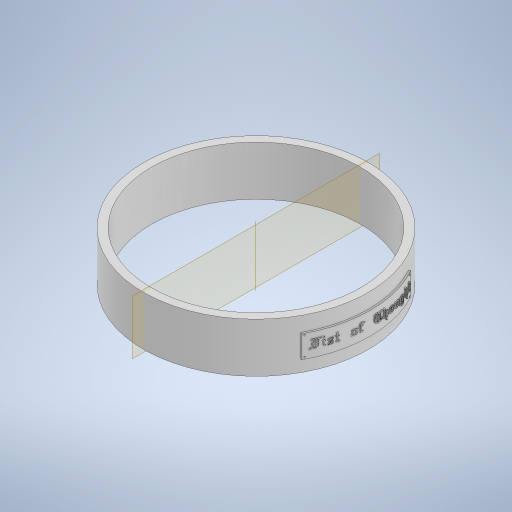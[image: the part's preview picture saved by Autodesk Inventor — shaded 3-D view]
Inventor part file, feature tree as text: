
AUTODESK INVENTOR PART (.ipt)
format: ipt  version: 2023 (Build 270158000, 158)  size: 5,846,016 bytes
history: native  units: in
note: dims shown in document units (in); Inventor stores cm internally (conversion verified against a paired STEP export)
features: emboss x3, pattern_circular x3, other x2, extrude x1, plane x1, fillet x1, sketch x1
ambient origin geometry x8: Origin, YZ Plane, XZ Plane, XY Plane, X Axis, Y Axis, Z Axis, Center Point
bodies: Solid1 (feature_tree)
feature tree (12):
  extrude  "Extrusion1"  Depth=1.9685in
  plane  "Work Plane1"
  other  "Text"
  emboss  "Emboss4"
  emboss  "Emboss5"
  emboss  "Emboss6"
  fillet  "Rivots"  Radius=0.8661in
  pattern_circular  "Circular Pattern1"  Count=6  [1 undecoded]
  pattern_circular  "Circular Pattern2"  [2 undecoded]
  pattern_circular  "Circular Pattern3"  [2 undecoded]
  sketch  "Sketch1"  dims[d0=3.937in d1=3.6614in d2=0.8661in d3=0.0in d4=2.3622in d6=0.4546in d10=0.0in d11=0.3937in d12=1.9685in d19=0.0in d20=0.0in d21=0.0295in d22=0.0in d23=0.0197in d24=0.0in d25=0.0295in d26=0.0295in d27=0.0295in d28=0.0157in d29=0.0in d30=0.0138in d31=0.7874in d32=360.0deg d34=0.7874in d35=360.0deg d37=0.7874in d38=360.0deg d33=0.0in]
  other  "NamePlate"
note: 5 required parameter values undecoded (feature->parameter linkage not recoverable at this tier; creation-order binding heuristic only, values carry confidence <= 0.55)
